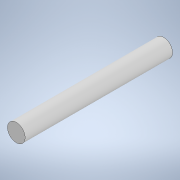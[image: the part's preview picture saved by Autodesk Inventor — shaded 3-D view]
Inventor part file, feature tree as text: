
AUTODESK INVENTOR PART (.ipt)
format: ipt  version: 2022 (Build 260153000, 153)  size: 92,672 bytes
history: native  units: mm
features: sketch x2, extrude x1
ambient origin geometry x8: Origin, YZ Plane, XZ Plane, XY Plane, X Axis, Y Axis, Z Axis, Center Point
bodies: Solid1 (feature_tree)
feature tree (3):
  sketch  "Sketch1"  dims[d0=6.0mm d1=50.0mm]
  extrude  "Extrusion1"  Depth=50.0mm
  sketch  "Sketch2"  dims[d2=0.0mm]
